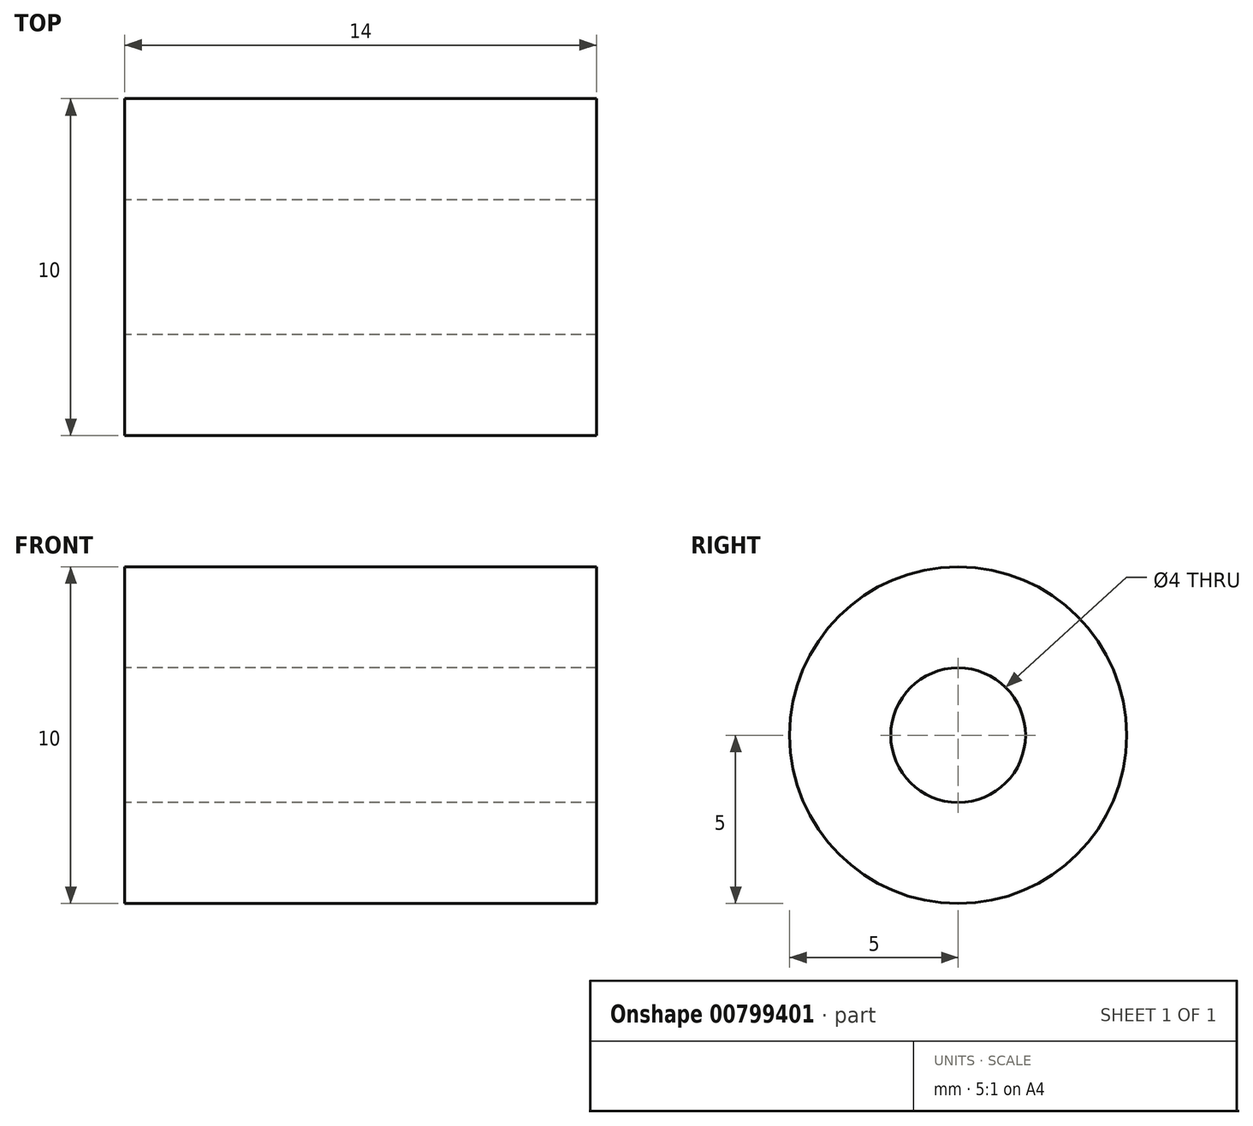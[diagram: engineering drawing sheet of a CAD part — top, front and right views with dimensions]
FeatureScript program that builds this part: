
annotation { "Feature Type Name" : "Feature", "Feature Type Description" : "" }
export const myFeature = defineFeature(function(context is Context, id is Id, definition is map)
    precondition{}
    {
        {
            var Q0;
            Q0=qCreatedBy(makeId("Right.planeOp"),FACE);
            var sketch = newSketch(context, id + "F0", { "sketchPlane" : qUnion([Q0])});
            skCircle(sketch, "E0", {"center": v(0, 0) * mm, "radius": 5 * mm});
            skCircle(sketch, "E1", {"center": v(0, 0) * mm, "radius": 2 * mm});
            skSolve(sketch);
        }
        {
            var Q0;
            Q0 = qSketchRegion(id + "F0", true);
            extrude(context, id + "F1", {"entities" : qUnion([Q0]), "endBound" : BoundingType.SYMMETRIC, "depth" : 14 * mm, "offsetDistance" : 25 * mm});
        }
    });
